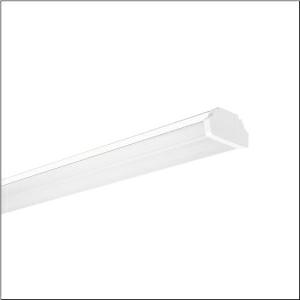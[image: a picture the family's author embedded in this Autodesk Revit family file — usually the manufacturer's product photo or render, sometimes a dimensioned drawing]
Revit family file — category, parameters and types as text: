
# Revit family: modario_31_gen_2_53bm812cv685c2_9c12
name_source: partatom
category: Lighting Fixtures
units: mm (PartAtom-declared; Revit-internal decimal feet)

## family parameters
Cut with Voids When Loaded = No
Host = Face
Light Source = No
Part Type = Normal
Room Calculation Point = No
Round Connector Dimension = Use Diameter
Shared = No

## types (1)
- --- (1 x LED, 8970 lm, 49.9 W, 6500K)
    Apparent Load = 50 VA
    CIE Flux Codes = 47 80 95 93 100
    Color Rendering = 80
    Color Temperature = 6500K
    Default Elevation = 1800 mm
    Description = Modario 31 Gen.2, luminaire insert, of sheet steel, coil coated, white, length: 1.495mm, width: 81mm, height: 82mm, 5x system unit, system units: 299mm, LED rated luminous flux: 8.970lm, light colour: 865, SDCM (Standard Deviation of Colour Matching)MacAdam ≤ 3 SDCM (initial), control gear: ON/OFF Multilumen, CLOi, with plug, 3-pole, with phase selection, mains connection: 220..240V, AC, 50/60Hz, start of lifetime: 50W, end of service life: 61W, through-wiring accessed according to module size, primary optical cover: cover, of PMMA, light emission: direct distribution, primary light characteristic: symmetric, protection rating (complete): IP20, protection rating (LED compartment): IP50, insulation class (complete): insulation class I (protective earthing), certification: CE, ENEC, VDE, UKCA, impact resistance: IK03, permissible ambient temperature for indoor applications: -35..+40°C, corresponds to IFS (International Featured Standards) requirements for safety and quality in the food industry, reducing of maximum allowable ambient temperature of 5°C with ceiling mounting, IP40 when using the optional accessory 5TP9018, packaging unit: 1 piece
    Height = 92 mm
    Lamp = 1 x LED
    Lamp Light Flux = 8970 lm
    Lamp Power = 49.9 W
    Lamp count = 1
    Length = 1495 mm
    Luminous efficacy = 180 lm/W
    Manufacturer = Siteco
    ModVariant = No
    Model = 53BM812CV685C2
    Mounting Place = Ceiling
    Mounting Type = Pendant
    Number of Poles = 1
    OnlyDefault = Yes
    Power Factor = 1
    Product Name = Modario 31 Gen.2
    Product group = luminaire insert | ceiling pendant
    ProductGroupID = 901
    Protection Class = Protection class I
    Protection Degree = IP 20
    RLX_Detail_Level = 1
    RLX_Emergency_Light_Flux = 0 lm
    RLX_Emergency_Type = 0
    RLX_Emergency_Type_DB = No
    RlxData = <blob elided: 39917 chars, md5=ea1ba438>
    Socket = socket
    Standby Power = 0 W
    System Light Flux = 8970 lm
    System Power = 50 W
    Type Comments = factory setting: luminous flux: 100 % | (A | C | E) | 116 mA
    Type Image = l_1341886.jpg
    URL = http://relux.com
    VarID = @adj_052331
    Voltage = 0 V
    Weight = 0.00 kg
    Width = 81 mm

## geometry (parser evidence)
native form markers: Blend x4, Sweep x12
no freeform markers — native parametric forms only
